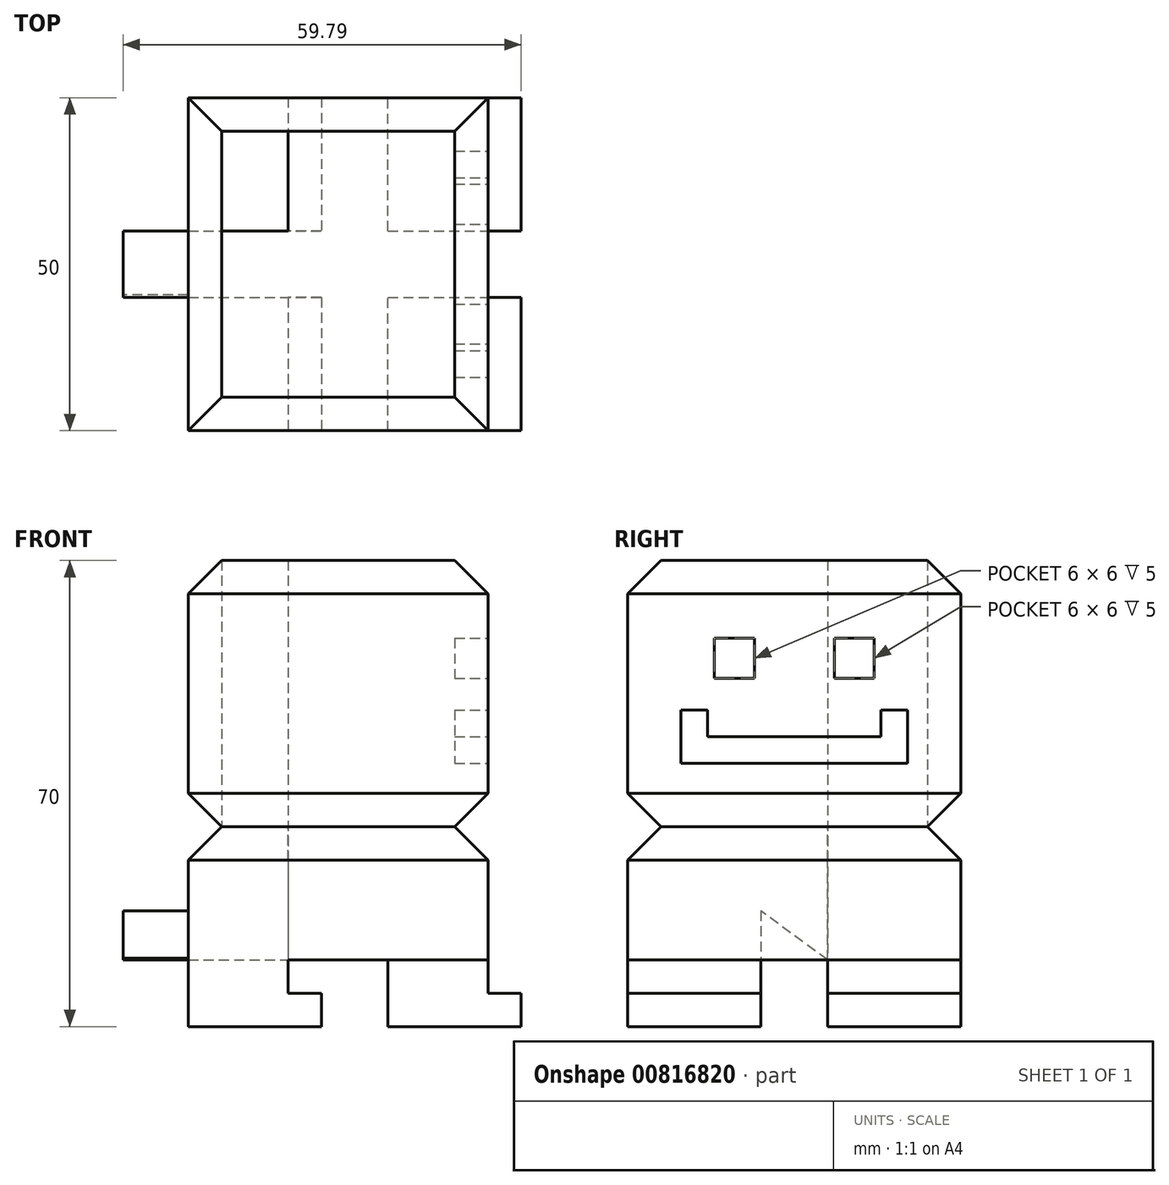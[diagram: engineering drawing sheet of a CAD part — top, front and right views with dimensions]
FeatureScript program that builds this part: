
annotation { "Feature Type Name" : "Feature", "Feature Type Description" : "" }
export const myFeature = defineFeature(function(context is Context, id is Id, definition is map)
    precondition{}
    {
        {
            var Q0;
            Q0=qCreatedBy(makeId("Top.planeOp"),FACE);
            var sketch = newSketch(context, id + "F0", { "sketchPlane" : qUnion([Q0])});
            skLineSegment(sketch, "E0.bottom", {"start": v(9.79, -45.15) * mm, "end": v(29.79, -45.15) * mm});
            skLineSegment(sketch, "E0.top", {"start": v(9.79, -25.15) * mm, "end": v(29.79, -25.15) * mm});
            skLineSegment(sketch, "E0.left", {"start": v(9.79, -45.15) * mm, "end": v(9.79, -25.15) * mm});
            skLineSegment(sketch, "E0.right", {"start": v(29.79, -45.15) * mm, "end": v(29.79, -25.15) * mm});
            skLineSegment(sketch, "E1.0.1.0", {"start": v(29.79, -15.15) * mm, "end": v(29.79, 4.85) * mm});
            skLineSegment(sketch, "E1.0.1.1", {"start": v(9.79, -15.15) * mm, "end": v(9.79, 4.85) * mm});
            skLineSegment(sketch, "E1.0.1.2", {"start": v(9.79, 4.85) * mm, "end": v(29.79, 4.85) * mm});
            skLineSegment(sketch, "E1.0.1.3", {"start": v(9.79, -15.15) * mm, "end": v(29.79, -15.15) * mm});
            skLineSegment(sketch, "E1.1.0.0", {"start": v(59.79, -45.15) * mm, "end": v(59.79, -25.15) * mm});
            skLineSegment(sketch, "E1.1.0.1", {"start": v(39.79, -45.15) * mm, "end": v(39.79, -25.15) * mm});
            skLineSegment(sketch, "E1.1.0.2", {"start": v(39.79, -25.15) * mm, "end": v(59.79, -25.15) * mm});
            skLineSegment(sketch, "E1.1.0.3", {"start": v(39.79, -45.15) * mm, "end": v(59.79, -45.15) * mm});
            skLineSegment(sketch, "E1.1.1.0", {"start": v(59.79, -15.15) * mm, "end": v(59.79, 4.85) * mm});
            skLineSegment(sketch, "E1.1.1.1", {"start": v(39.79, -15.15) * mm, "end": v(39.79, 4.85) * mm});
            skLineSegment(sketch, "E1.1.1.2", {"start": v(39.79, 4.85) * mm, "end": v(59.79, 4.85) * mm});
            skLineSegment(sketch, "E1.1.1.3", {"start": v(39.79, -15.15) * mm, "end": v(59.79, -15.15) * mm});
            skLineSegment(sketch, "E1.direction1", {"start": v(9.79, -45.15) * mm, "end": v(39.79, -45.15) * mm, "construction": true});
            skLineSegment(sketch, "E1.direction2", {"start": v(9.79, -45.15) * mm, "end": v(9.79, -15.15) * mm, "construction": true});
            skSolve(sketch);
        }
        {
            var Q0;
            Q0 = qSketchRegion(id + "F0", true);
            extrude(context, id + "F1", {"entities" : qUnion([Q0]), "depth" : 10 * mm, "offsetDistance" : 25 * mm});
        }
        {
            var Q0;
            Q0=makeQuery(id+"F1.opExtrude","CAP_FACE",FACE,{"disambiguationData":[OSD([sQuery(id+"F0.wireOp",EDGE,"E1.1.0.0"),sQuery(id+"F0.wireOp",EDGE,"E1.1.0.1"),sQuery(id+"F0.wireOp",EDGE,"E1.1.0.2"),sQuery(id+"F0.wireOp",EDGE,"E1.1.0.3")])],"isStart":false});
            var sketch = newSketch(context, id + "F2", { "sketchPlane" : qUnion([Q0])});
            skLineSegment(sketch, "E2.bottom", {"start": v(59.79, -25.15) * mm, "end": v(54.79, -25.15) * mm});
            skLineSegment(sketch, "E2.top", {"start": v(59.79, -45.15) * mm, "end": v(54.79, -45.15) * mm});
            skLineSegment(sketch, "E2.left", {"start": v(59.79, -25.15) * mm, "end": v(59.79, -45.15) * mm});
            skLineSegment(sketch, "E2.right", {"start": v(54.79, -25.15) * mm, "end": v(54.79, -45.15) * mm});
            skLineSegment(sketch, "E3.0.1.0", {"start": v(54.79, 4.85) * mm, "end": v(54.79, -15.15) * mm});
            skLineSegment(sketch, "E3.0.1.1", {"start": v(59.79, 4.85) * mm, "end": v(54.79, 4.85) * mm});
            skLineSegment(sketch, "E3.0.1.2", {"start": v(59.79, 4.85) * mm, "end": v(59.79, -15.15) * mm});
            skLineSegment(sketch, "E3.0.1.3", {"start": v(59.79, -15.15) * mm, "end": v(54.79, -15.15) * mm});
            skLineSegment(sketch, "E3.1.0.0", {"start": v(24.79, -25.15) * mm, "end": v(24.79, -45.15) * mm});
            skLineSegment(sketch, "E3.1.0.1", {"start": v(29.79, -25.15) * mm, "end": v(24.79, -25.15) * mm});
            skLineSegment(sketch, "E3.1.0.2", {"start": v(29.79, -25.15) * mm, "end": v(29.79, -45.15) * mm});
            skLineSegment(sketch, "E3.1.0.3", {"start": v(29.79, -45.15) * mm, "end": v(24.79, -45.15) * mm});
            skLineSegment(sketch, "E3.1.1.0", {"start": v(24.79, 4.85) * mm, "end": v(24.79, -15.15) * mm});
            skLineSegment(sketch, "E3.1.1.1", {"start": v(29.79, 4.85) * mm, "end": v(24.79, 4.85) * mm});
            skLineSegment(sketch, "E3.1.1.2", {"start": v(29.79, 4.85) * mm, "end": v(29.79, -15.15) * mm});
            skLineSegment(sketch, "E3.1.1.3", {"start": v(29.79, -15.15) * mm, "end": v(24.79, -15.15) * mm});
            skLineSegment(sketch, "E3.direction1", {"start": v(54.79, -45.15) * mm, "end": v(24.79, -45.15) * mm, "construction": true});
            skLineSegment(sketch, "E3.direction2", {"start": v(54.79, -45.15) * mm, "end": v(54.79, -15.15) * mm, "construction": true});
            skSolve(sketch);
        }
        {
            var Q0;
            Q0 = qSketchRegion(id + "F2", true);
            extrude(context, id + "F3", {"entities" : qUnion([Q0]), "operationType" : NewBodyOperationType.REMOVE, "oppositeDirection" : true, "depth" : 5 * mm, "offsetDistance" : 25 * mm});
        }
        {
            var Q0;
            Q0=makeQuery(id+"F1.opExtrude","CAP_FACE",FACE,{"disambiguationData":[OSD([sQuery(id+"F0.wireOp",EDGE,"E1.0.1.0"),sQuery(id+"F0.wireOp",EDGE,"E1.0.1.1"),sQuery(id+"F0.wireOp",EDGE,"E1.0.1.2"),sQuery(id+"F0.wireOp",EDGE,"E1.0.1.3")])],"isStart":false});
            var sketch = newSketch(context, id + "F4", { "sketchPlane" : qUnion([Q0])});
            skLineSegment(sketch, "E4.bottom", {"start": v(9.79, 4.85) * mm, "end": v(54.79, 4.85) * mm});
            skLineSegment(sketch, "E4.top", {"start": v(9.79, -45.15) * mm, "end": v(54.79, -45.15) * mm});
            skLineSegment(sketch, "E4.left", {"start": v(9.79, 4.85) * mm, "end": v(9.79, -45.15) * mm});
            skLineSegment(sketch, "E4.right", {"start": v(54.79, 4.85) * mm, "end": v(54.79, -45.15) * mm});
            skSolve(sketch);
        }
        {
            var Q0;
            {var subQ3=sQuery(id+"F4.wireOp",EDGE,"E4.top");Q0=makeQuery(id+"F4.imprint","IMPRINT",FACE,{"disambiguationData":[TD([[makeQuery(id+"F4.imprint","IMPRINT",EDGE,{"derivedFrom":subQ3}),1.0]])]});}
            var Q1;
            {var subQ3=makeQuery(id+"F3.boolean.opBoolean","COPY",EDGE,{"derivedFrom":makeQuery(id+"F3.opExtrude","CAP_EDGE",EDGE,{"disambiguationData":[OSD([sQuery(id+"F2.wireOp",EDGE,"E3.1.1.0")])],"isStart":true})});Q1=makeQuery(id+"F4.imprint","IMPRINT",FACE,{"disambiguationData":[TD([[makeQuery(id+"F4.imprint","IMPRINT",EDGE,{"derivedFrom":subQ3}),-1.0]])]});}
            extrude(context, id + "F5", {"entities" : qUnion([Q0, Q1]), "depth" : 20 * mm, "offsetDistance" : 25 * mm});
        }
        {
            var Q0;
            Q0=makeQuery(id+"F5.opExtrude","CAP_EDGE",EDGE,{"disambiguationData":[OSD([sQuery(id+"F4.wireOp",EDGE,"E4.bottom")])],"isStart":false});
            var Q1;
            Q1=makeQuery(id+"F5.opExtrude","CAP_EDGE",EDGE,{"disambiguationData":[OSD([sQuery(id+"F4.wireOp",EDGE,"E4.right")])],"isStart":false});
            var Q2;
            Q2=makeQuery(id+"F5.opExtrude","CAP_EDGE",EDGE,{"disambiguationData":[OSD([sQuery(id+"F4.wireOp",EDGE,"E4.top")])],"isStart":false});
            var Q3;
            Q3=makeQuery(id+"F5.opExtrude","CAP_EDGE",EDGE,{"disambiguationData":[OSD([sQuery(id+"F4.wireOp",EDGE,"E4.left")])],"isStart":false});
            chamfer(context, id + "F6", {"entities" : qUnion([Q0, Q1, Q2, Q3]), "width" : 5 * mm, "tangentPropagation" : true});
        }
        {
            var Q0;
            Q0=makeQuery(id+"F5.opExtrude","CAP_FACE",FACE,{"disambiguationData":[OSD([sQuery(id+"F4.wireOp",EDGE,"E4.bottom"),sQuery(id+"F4.wireOp",EDGE,"E4.top"),sQuery(id+"F4.wireOp",EDGE,"E4.left"),sQuery(id+"F4.wireOp",EDGE,"E4.right")])],"isStart":false});
            var sketch = newSketch(context, id + "F7", { "sketchPlane" : qUnion([Q0])});
            skLineSegment(sketch, "E5.bottom", {"start": v(14.79, -0.15) * mm, "end": v(49.79, -0.15) * mm});
            skLineSegment(sketch, "E5.top", {"start": v(14.79, -40.15) * mm, "end": v(49.79, -40.15) * mm});
            skLineSegment(sketch, "E5.left", {"start": v(14.79, -0.15) * mm, "end": v(14.79, -40.15) * mm});
            skLineSegment(sketch, "E5.right", {"start": v(49.79, -0.15) * mm, "end": v(49.79, -40.15) * mm});
            skLineSegment(sketch, "E6.0", {"start": v(54.79, 4.85) * mm, "end": v(9.79, 4.85) * mm});
            skLineSegment(sketch, "E6.1", {"start": v(54.79, -45.15) * mm, "end": v(54.79, 4.85) * mm});
            skLineSegment(sketch, "E6.2", {"start": v(9.79, -45.15) * mm, "end": v(54.79, -45.15) * mm});
            skLineSegment(sketch, "E6.3", {"start": v(9.79, 4.85) * mm, "end": v(9.79, -45.15) * mm});
            skSolve(sketch);
        }
        {
            var Q0;
            Q0 = qSketchRegion(id + "F7", true);
            var Q1;
            Q1=makeQuery(id+"F7.imprint","IMPRINT",FACE,{"disambiguationData":[TD([[makeQuery(id+"F7.imprint","IMPRINT",EDGE,{"derivedFrom":sQuery(id+"F7.wireOp",EDGE,"E5.bottom")}),1.0]])]});
            extrude(context, id + "F8", {"entities" : qUnion([Q0, Q1]), "operationType" : NewBodyOperationType.ADD, "depth" : 40 * mm, "offsetDistance" : 25 * mm});
        }
        {
            var Q0;
            Q0=makeQuery(id+"F8.opExtrude","CAP_EDGE",EDGE,{"disambiguationData":[OSD([sQuery(id+"F7.wireOp",EDGE,"E6.2")])],"isStart":true});
            var Q1;
            Q1=makeQuery(id+"F8.opExtrude","CAP_EDGE",EDGE,{"disambiguationData":[OSD([sQuery(id+"F7.wireOp",EDGE,"E6.1")])],"isStart":true});
            var Q2;
            Q2=makeQuery(id+"F8.opExtrude","CAP_EDGE",EDGE,{"disambiguationData":[OSD([sQuery(id+"F7.wireOp",EDGE,"E6.0")])],"isStart":true});
            var Q3;
            Q3=makeQuery(id+"F8.opExtrude","CAP_EDGE",EDGE,{"disambiguationData":[OSD([sQuery(id+"F7.wireOp",EDGE,"E6.3")])],"isStart":true});
            chamfer(context, id + "F9", {"entities" : qUnion([Q0, Q1, Q2, Q3]), "width" : 5 * mm, "tangentPropagation" : true});
        }
        {
            var Q0;
            Q0=makeQuery(id+"F8.opExtrude","CAP_EDGE",EDGE,{"disambiguationData":[OSD([sQuery(id+"F7.wireOp",EDGE,"E6.2")])],"isStart":false});
            var Q1;
            Q1=makeQuery(id+"F8.opExtrude","CAP_EDGE",EDGE,{"disambiguationData":[OSD([sQuery(id+"F7.wireOp",EDGE,"E6.1")])],"isStart":false});
            var Q2;
            Q2=makeQuery(id+"F8.opExtrude","CAP_EDGE",EDGE,{"disambiguationData":[OSD([sQuery(id+"F7.wireOp",EDGE,"E6.0")])],"isStart":false});
            var Q3;
            Q3=makeQuery(id+"F8.opExtrude","CAP_EDGE",EDGE,{"disambiguationData":[OSD([sQuery(id+"F7.wireOp",EDGE,"E6.3")])],"isStart":false});
            chamfer(context, id + "F10", {"entities" : qUnion([Q0, Q1, Q2, Q3]), "width" : 5 * mm, "tangentPropagation" : true});
        }
        {
            var Q0;
            Q0=makeQuery(id+"F8.opExtrude","SWEPT_FACE",FACE,{"disambiguationData":[OSD([sQuery(id+"F7.wireOp",EDGE,"E6.1")])]});
            var sketch = newSketch(context, id + "F11", { "sketchPlane" : qUnion([Q0])});
            skLineSegment(sketch, "E7.bottom", {"start": v(-32.15, 58.3) * mm, "end": v(-26.15, 58.3) * mm});
            skLineSegment(sketch, "E7.top", {"start": v(-32.15, 52.3) * mm, "end": v(-26.15, 52.3) * mm});
            skLineSegment(sketch, "E7.left", {"start": v(-32.15, 58.3) * mm, "end": v(-32.15, 52.3) * mm});
            skLineSegment(sketch, "E7.right", {"start": v(-26.15, 58.3) * mm, "end": v(-26.15, 52.3) * mm});
            skLineSegment(sketch, "E8.bottom", {"start": v(-14.15, 58.3) * mm, "end": v(-8.15, 58.3) * mm});
            skLineSegment(sketch, "E8.top", {"start": v(-14.15, 52.3) * mm, "end": v(-8.15, 52.3) * mm});
            skLineSegment(sketch, "E8.left", {"start": v(-14.15, 58.3) * mm, "end": v(-14.15, 52.3) * mm});
            skLineSegment(sketch, "E8.right", {"start": v(-8.15, 58.3) * mm, "end": v(-8.15, 52.3) * mm});
            skLineSegment(sketch, "E9.bottom", {"start": v(-37.15, 47.53) * mm, "end": v(-33.15, 47.53) * mm});
            skLineSegment(sketch, "E9.top", {"start": v(-37.15, 39.53) * mm, "end": v(-33.15, 39.53) * mm});
            skLineSegment(sketch, "E9.left", {"start": v(-37.15, 47.53) * mm, "end": v(-37.15, 39.53) * mm});
            skLineSegment(sketch, "E9.right", {"start": v(-33.15, 47.53) * mm, "end": v(-33.15, 39.53) * mm});
            skLineSegment(sketch, "E10.bottom", {"start": v(-33.15, 43.53) * mm, "end": v(-7.15, 43.53) * mm});
            skLineSegment(sketch, "E10.top", {"start": v(-33.15, 39.53) * mm, "end": v(-7.15, 39.53) * mm});
            skLineSegment(sketch, "E10.left", {"start": v(-33.15, 43.53) * mm, "end": v(-33.15, 39.53) * mm});
            skLineSegment(sketch, "E10.right", {"start": v(-7.15, 43.53) * mm, "end": v(-7.15, 39.53) * mm});
            skLineSegment(sketch, "E11.bottom", {"start": v(-7.15, 47.53) * mm, "end": v(-3.15, 47.53) * mm});
            skLineSegment(sketch, "E11.top", {"start": v(-7.15, 39.53) * mm, "end": v(-3.15, 39.53) * mm});
            skLineSegment(sketch, "E11.left", {"start": v(-7.15, 47.53) * mm, "end": v(-7.15, 39.53) * mm});
            skLineSegment(sketch, "E11.right", {"start": v(-3.15, 47.53) * mm, "end": v(-3.15, 39.53) * mm});
            skLineSegment(sketch, "E12", {"start": v(-20.15, 65) * mm, "end": v(-20.15, 35) * mm, "construction": true});
            skSolve(sketch);
        }
        {
            var Q0;
            Q0 = qSketchRegion(id + "F11", true);
            extrude(context, id + "F12", {"entities" : qUnion([Q0]), "operationType" : NewBodyOperationType.REMOVE, "oppositeDirection" : true, "depth" : 5 * mm, "offsetDistance" : 25 * mm});
        }
        {
            var Q0;
            Q0=qCreatedBy(makeId("Top.planeOp"),FACE);
            cPlane(context, id + "F13", {"entities" : qUnion([Q0]), "cplaneType" : CPlaneType.OFFSET, "offset" : 10 * mm, "width" : 150 * mm, "height" : 150 * mm});
        }
        {
            var Q0;
            Q0=qCreatedBy(id+"F13.planeOp",FACE);
            var sketch = newSketch(context, id + "F14", { "sketchPlane" : qUnion([Q0])});
            skLineSegment(sketch, "E13.bottom", {"start": v(9.79, -15.15) * mm, "end": v(0, -15.15) * mm});
            skLineSegment(sketch, "E13.top", {"start": v(9.79, -25.15) * mm, "end": v(0, -25.15) * mm});
            skLineSegment(sketch, "E13.left", {"start": v(9.79, -15.15) * mm, "end": v(9.79, -25.15) * mm});
            skLineSegment(sketch, "E13.right", {"start": v(0, -15.15) * mm, "end": v(0, -25.15) * mm});
            skLineSegment(sketch, "E14.bottom", {"start": v(0, -25.15) * mm, "end": v(9.79, -25.15) * mm});
            skLineSegment(sketch, "E14.top", {"start": v(0, -45.15) * mm, "end": v(9.79, -45.15) * mm});
            skLineSegment(sketch, "E14.left", {"start": v(0, -25.15) * mm, "end": v(0, -45.15) * mm});
            skLineSegment(sketch, "E14.right", {"start": v(9.79, -25.15) * mm, "end": v(9.79, -45.15) * mm});
            skSolve(sketch);
        }
        {
            var Q0;
            Q0=makeQuery(id+"F5.opExtrude","SWEPT_FACE",FACE,{"disambiguationData":[OSD([sQuery(id+"F4.wireOp",EDGE,"E4.left")])]});
            var sketch = newSketch(context, id + "F15", { "sketchPlane" : qUnion([Q0])});
            skLineSegment(sketch, "E15", {"start": v(25.2, 10) * mm, "end": v(45.15, 25) * mm});
            skLineSegment(sketch, "E16", {"start": v(15.15, 10) * mm, "end": v(35.15, 25) * mm});
            skLineSegment(sketch, "E17", {"start": v(35.15, 25) * mm, "end": v(45.15, 25) * mm});
            skLineSegment(sketch, "E18", {"start": v(25.2, 10) * mm, "end": v(15.15, 10) * mm});
            skSolve(sketch);
        }
        {
            var Q0;
            Q0=makeQuery(id+"F14.imprint","IMPRINT",FACE,{"disambiguationData":[TD([[makeQuery(id+"F14.imprint","IMPRINT",EDGE,{"derivedFrom":sQuery(id+"F14.wireOp",EDGE,"E13.bottom")}),1.0]])]});
            var Q1;
            Q1=makeQuery(id+"F14.imprint","IMPRINT",FACE,{"disambiguationData":[TD([[makeQuery(id+"F14.imprint","IMPRINT",EDGE,{"derivedFrom":sQuery(id+"F14.wireOp",EDGE,"E14.bottom")}),-1.0]])]});
            extrude(context, id + "F16", {"entities" : qUnion([Q0, Q1]), "operationType" : NewBodyOperationType.ADD, "depth" : 15 * mm, "offsetDistance" : 25 * mm});
        }
        {
            var Q0;
            Q0=makeQuery(id+"F16.opExtrude","SWEPT_FACE",FACE,{"disambiguationData":[OSD([sQuery(id+"F14.wireOp",EDGE,"E13.right"),sQuery(id+"F14.wireOp",EDGE,"E14.left")])]});
            var sketch = newSketch(context, id + "F17", { "sketchPlane" : qUnion([Q0])});
            skLineSegment(sketch, "E19", {"start": v(15.15, 10) * mm, "end": v(35.52, 25) * mm});
            skLineSegment(sketch, "E20", {"start": v(35.52, 25) * mm, "end": v(45.15, 25) * mm});
            skLineSegment(sketch, "E21", {"start": v(45.15, 25) * mm, "end": v(24.78, 10) * mm});
            skLineSegment(sketch, "E22", {"start": v(24.78, 10) * mm, "end": v(15.15, 10) * mm});
            skSolve(sketch);
        }
        {
            var Q0;
            Q0=makeQuery(id+"F16.boolean.opBoolean","MERGE",FACE,{"derivedFrom":[makeQuery(id+"F5.opExtrude","SWEPT_FACE",FACE,{"disambiguationData":[OSD([sQuery(id+"F4.wireOp",EDGE,"E4.top")])]}),makeQuery(id+"F16.opExtrude","SWEPT_FACE",FACE,{"disambiguationData":[OSD([sQuery(id+"F14.wireOp",EDGE,"E14.top")])]})]});
            var sketch = newSketch(context, id + "F18", { "sketchPlane" : qUnion([Q0])});
            skLineSegment(sketch, "E23.bottom", {"start": v(5, 25) * mm, "end": v(9.79, 25) * mm});
            skLineSegment(sketch, "E23.top", {"start": v(5, 15) * mm, "end": v(9.79, 15) * mm});
            skLineSegment(sketch, "E23.left", {"start": v(5, 25) * mm, "end": v(5, 15) * mm});
            skLineSegment(sketch, "E23.right", {"start": v(9.79, 25) * mm, "end": v(9.79, 15) * mm});
            skSolve(sketch);
        }
        {
            var Q0;
            Q0=makeQuery(id+"F18.imprint","IMPRINT",FACE,{"disambiguationData":[TD([[makeQuery(id+"F18.imprint","IMPRINT",EDGE,{"derivedFrom":sQuery(id+"F18.wireOp",EDGE,"E23.bottom")}),-1.0]])]});
            extrude(context, id + "F19", {"entities" : qUnion([Q0]), "operationType" : NewBodyOperationType.REMOVE, "endBound" : BoundingType.UP_TO_NEXT, "oppositeDirection" : true, "depth" : 25 * mm, "offsetDistance" : 25 * mm});
        }
        {
            var Q0;
            {var subQ0=sQuery(id+"F17.wireOp",EDGE,"E19");Q0=makeQuery(id+"F17.imprint","IMPRINT",FACE,{"disambiguationData":[TD([[makeQuery(id+"F17.imprint","IMPRINT",EDGE,{"derivedFrom":subQ0}),1.0]])]});}
            var Q1;
            {var subQ0=sQuery(id+"F17.wireOp",EDGE,"E21");Q1=makeQuery(id+"F17.imprint","IMPRINT",FACE,{"disambiguationData":[TD([[makeQuery(id+"F17.imprint","IMPRINT",EDGE,{"derivedFrom":subQ0}),1.0]])]});}
            var Q2;
            Q2=makeQuery(id+"F19.boolean.opBoolean","MERGE",FACE,{"derivedFrom":[makeQuery(id+"F5.opExtrude","SWEPT_FACE",FACE,{"disambiguationData":[OSD([sQuery(id+"F4.wireOp",EDGE,"E4.left")])]}),makeQuery(id+"F19.opExtrude","SWEPT_FACE",FACE,{"disambiguationData":[OSD([sQuery(id+"F18.wireOp",EDGE,"E23.right")])]})]});
            extrude(context, id + "F20", {"entities" : qUnion([Q0, Q1]), "operationType" : NewBodyOperationType.REMOVE, "endBound" : BoundingType.UP_TO_SURFACE, "oppositeDirection" : true, "depth" : 25 * mm, "endBoundEntityFace" : qUnion([Q2]), "offsetDistance" : 25 * mm});
        }
    });
